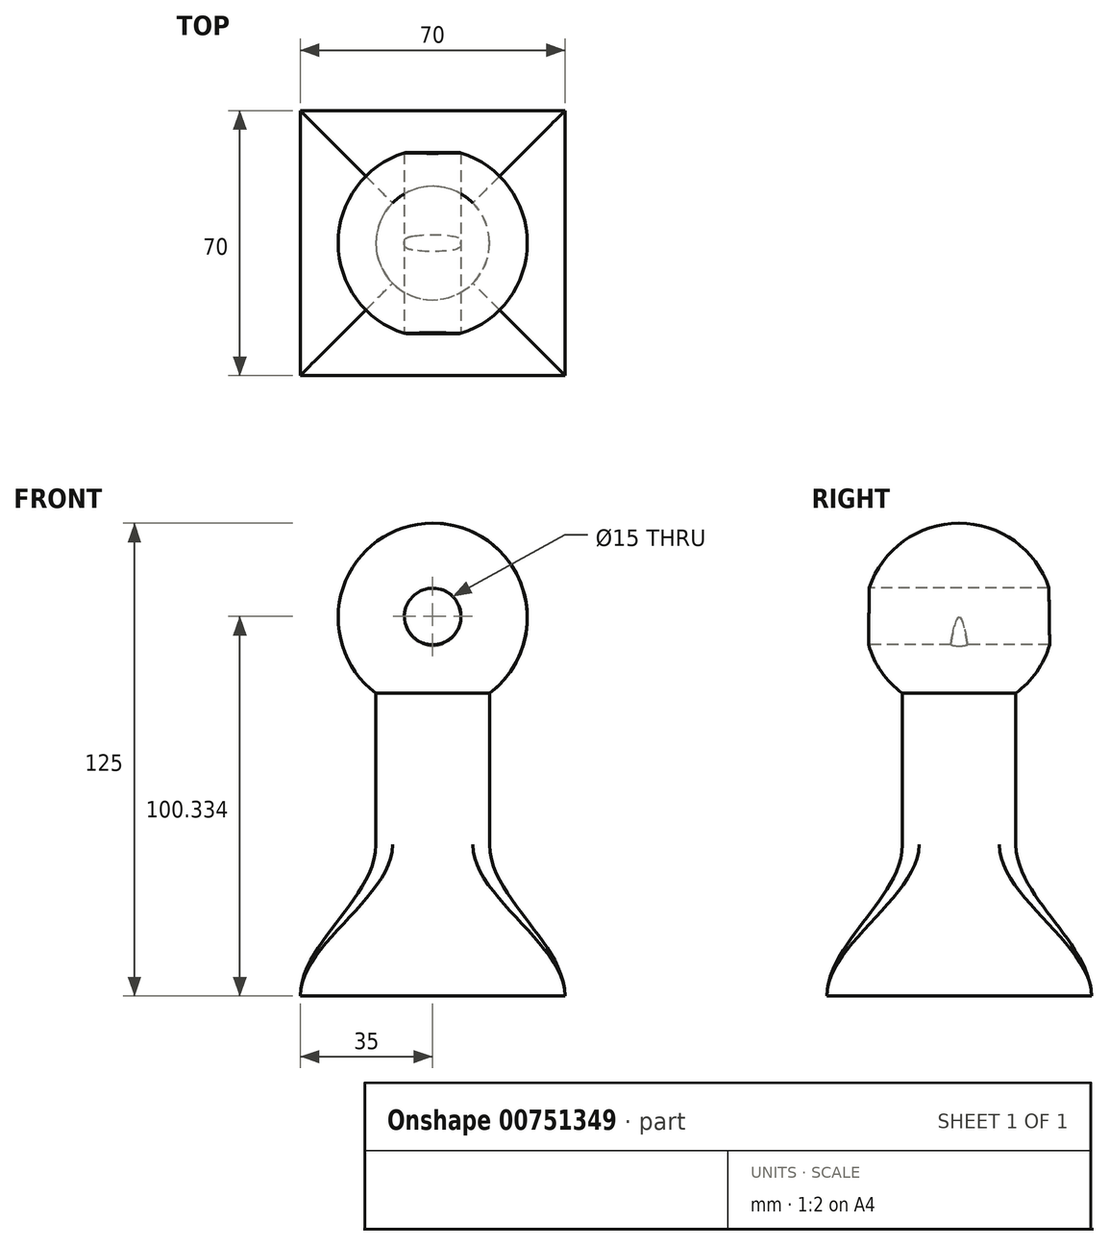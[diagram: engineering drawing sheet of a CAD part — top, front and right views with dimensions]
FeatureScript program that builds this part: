
annotation { "Feature Type Name" : "Feature", "Feature Type Description" : "" }
export const myFeature = defineFeature(function(context is Context, id is Id, definition is map)
    precondition{}
    {
        {
            var Q0;
            Q0=qCreatedBy(makeId("Front.planeOp"),FACE);
            var sketch = newSketch(context, id + "F0", { "sketchPlane" : qUnion([Q0])});
            skLineSegment(sketch, "E0", {"start": v(0, 0) * mm, "end": v(0, 40) * mm});
            skLineSegment(sketch, "E1", {"start": v(0, 40) * mm, "end": v(15, 40) * mm});
            skLineSegment(sketch, "E2", {"start": v(15, 40) * mm, "end": v(15, 0) * mm});
            skLineSegment(sketch, "E3", {"start": v(15, 0) * mm, "end": v(0, 0) * mm});
            skArc(sketch, "E4", {"start": v(15, 40) * mm, "mid": v(23.72, 67.9) * mm, "end": v(0, 85) * mm});
            skArc(sketch, "E5", {"start": v(0, 52.5) * mm, "mid": v(7.5, 60) * mm, "end": v(0, 67.5) * mm});
            skLineSegment(sketch, "E6", {"start": v(0, 40) * mm, "end": v(0, 52.5) * mm});
            skLineSegment(sketch, "E7", {"start": v(0, 0) * mm, "end": v(0, -16.6) * mm, "construction": true});
            skLineSegment(sketch, "E8.trimOffspring", {"start": v(0, 67.5) * mm, "end": v(0, 85) * mm});
            skSolve(sketch);
        }
        {
            var Q0;
            {var subQ0=sQuery(id+"F0.wireOp",EDGE,"E5");Q0=makeQuery(id+"F0.imprint","IMPRINT",FACE,{"disambiguationData":[TD([[makeQuery(id+"F0.imprint","IMPRINT",EDGE,{"derivedFrom":subQ0}),1.0]])]});}
            var Q1;
            {var subQ3=sQuery(id+"F0.wireOp",EDGE,"E1");Q1=makeQuery(id+"F0.imprint","IMPRINT",FACE,{"disambiguationData":[TD([[makeQuery(id+"F0.imprint","IMPRINT",EDGE,{"derivedFrom":subQ3}),1.0]])]});}
            var Q2;
            Q2=makeQuery(id+"F0.imprint","IMPRINT",FACE,{"disambiguationData":[TD([[makeQuery(id+"F0.imprint","IMPRINT",EDGE,{"derivedFrom":sQuery(id+"F0.wireOp",EDGE,"E0")}),-1.0]])]});
            var Q3;
            Q3=sQuery(id+"F0.wireOp",EDGE,"E7");
            revolve(context, id + "F1", {"surfaceOperationType" : NewSurfaceOperationType.NEW, "entities" : qUnion([Q0, Q1, Q2]), "axis" : qUnion([Q3]), "revolveType" : RevolveType.FULL});
        }
        {
            var Q0;
            Q0=makeQuery(id+"F1.opRevolve","SWEPT_FACE",FACE,{"disambiguationData":[OSD([sQuery(id+"F0.wireOp",EDGE,"E3")])]});
            cPlane(context, id + "F2", {"entities" : qUnion([Q0]), "cplaneType" : CPlaneType.OFFSET, "offset" : 40 * mm, "width" : 150 * mm, "height" : 150 * mm});
        }
        {
            var Q0;
            Q0=qCreatedBy(id+"F2.planeOp",FACE);
            var sketch = newSketch(context, id + "F3", { "sketchPlane" : qUnion([Q0])});
            skLineSegment(sketch, "E9.bottom", {"start": v(35, -35) * mm, "end": v(-35, -35) * mm});
            skLineSegment(sketch, "E9.top", {"start": v(35, 35) * mm, "end": v(-35, 35) * mm});
            skLineSegment(sketch, "E9.left", {"start": v(35, -35) * mm, "end": v(35, 35) * mm});
            skLineSegment(sketch, "E9.right", {"start": v(-35, -35) * mm, "end": v(-35, 35) * mm});
            skPoint(sketch, "E9.middle", {"position": v(0, 0) * mm});
            skSolve(sketch);
        }
        {
            var Q0;
            Q0=qCreatedBy(makeId("Front.planeOp"),FACE);
            var sketch = newSketch(context, id + "F4", { "sketchPlane" : qUnion([Q0])});
            skCircle(sketch, "E10", {"center": v(0, 60.33) * mm, "radius": 7.5 * mm});
            skSolve(sketch);
        }
        {
            var Q0;
            Q0 = qSketchRegion(id + "F4", true);
            var Q1;
            Q1=sQuery(id+"F4.wireOp",EDGE,"E10");
            extrude(context, id + "F5", {"entities" : qUnion([Q0]), "operationType" : NewBodyOperationType.REMOVE, "surfaceEntities" : qUnion([Q1]), "endBound" : BoundingType.THROUGH_ALL, "oppositeDirection" : true, "depth" : 25 * mm, "offsetDistance" : 25 * mm, "hasSecondDirection" : true, "secondDirectionBound" : SecondDirectionBoundingType.THROUGH_ALL, "secondDirectionOppositeDirection" : false, "secondDirectionDepth" : 25 * mm});
        }
        {
            var Q0;
            Q0=makeQuery(id+"F3.imprint","IMPRINT",FACE,{"disambiguationData":[TD([[makeQuery(id+"F3.imprint","IMPRINT",EDGE,{"derivedFrom":sQuery(id+"F3.wireOp",EDGE,"E9.bottom")}),-1.0]])]});
            var Q1;
            Q1=makeQuery(id+"F1.opRevolve","SWEPT_FACE",FACE,{"disambiguationData":[OSD([sQuery(id+"F0.wireOp",EDGE,"E3")])]});
            loft(context, id + "F6", {"operationType" : NewBodyOperationType.ADD, "startCondition" : LoftEndDerivativeType.NORMAL_TO_PROFILE, "startMagnitude" : 1, "endCondition" : LoftEndDerivativeType.NORMAL_TO_PROFILE, "endMagnitude" : 1, "sheetProfilesArray" : [{ "sheetProfileEntities" : qUnion([Q0]) }, { "sheetProfileEntities" : qUnion([Q1]) }]});
        }
    });
